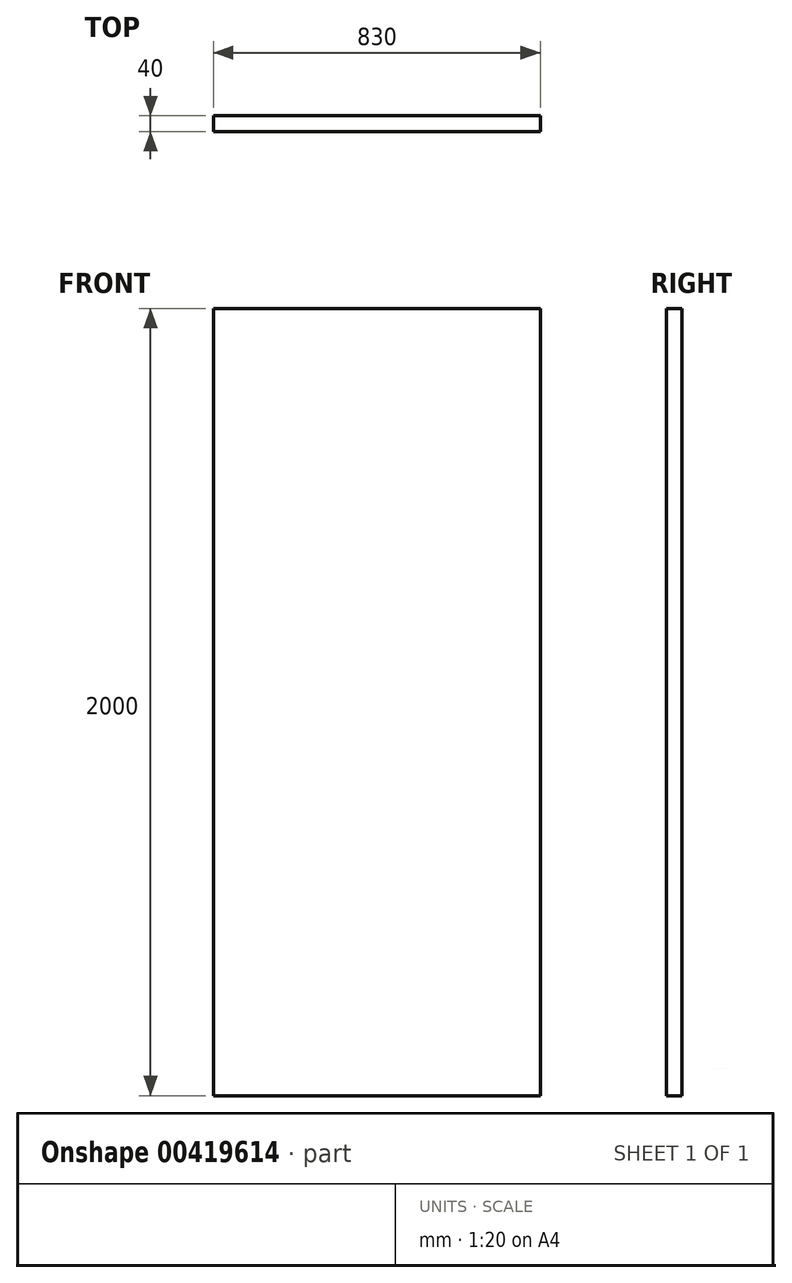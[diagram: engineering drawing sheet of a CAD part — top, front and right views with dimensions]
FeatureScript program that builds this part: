
annotation { "Feature Type Name" : "Feature", "Feature Type Description" : "" }
export const myFeature = defineFeature(function(context is Context, id is Id, definition is map)
    precondition{}
    {
        {
            var Q0;
            Q0=qCreatedBy(makeId("Top.planeOp"),FACE);
            var sketch = newSketch(context, id + "F0", { "sketchPlane" : qUnion([Q0])});
            skLineSegment(sketch, "E0.bottom", {"start": v(-74.47, 40) * mm, "end": v(755.53, 40) * mm});
            skLineSegment(sketch, "E0.top", {"start": v(-74.47, 0) * mm, "end": v(755.53, 0) * mm});
            skLineSegment(sketch, "E0.left", {"start": v(-74.47, 40) * mm, "end": v(-74.47, 0) * mm});
            skLineSegment(sketch, "E0.right", {"start": v(755.53, 40) * mm, "end": v(755.53, 0) * mm});
            skSolve(sketch);
        }
        {
            var Q0;
            Q0=makeQuery(id+"F0.imprint","IMPRINT",FACE,{"disambiguationData":[TD([[makeQuery(id+"F0.imprint","IMPRINT",EDGE,{"derivedFrom":sQuery(id+"F0.wireOp",EDGE,"E0.bottom")}),-1.0]])]});
            extrude(context, id + "F1", {"entities" : qUnion([Q0]), "depth" : 2000 * mm});
        }
    });
